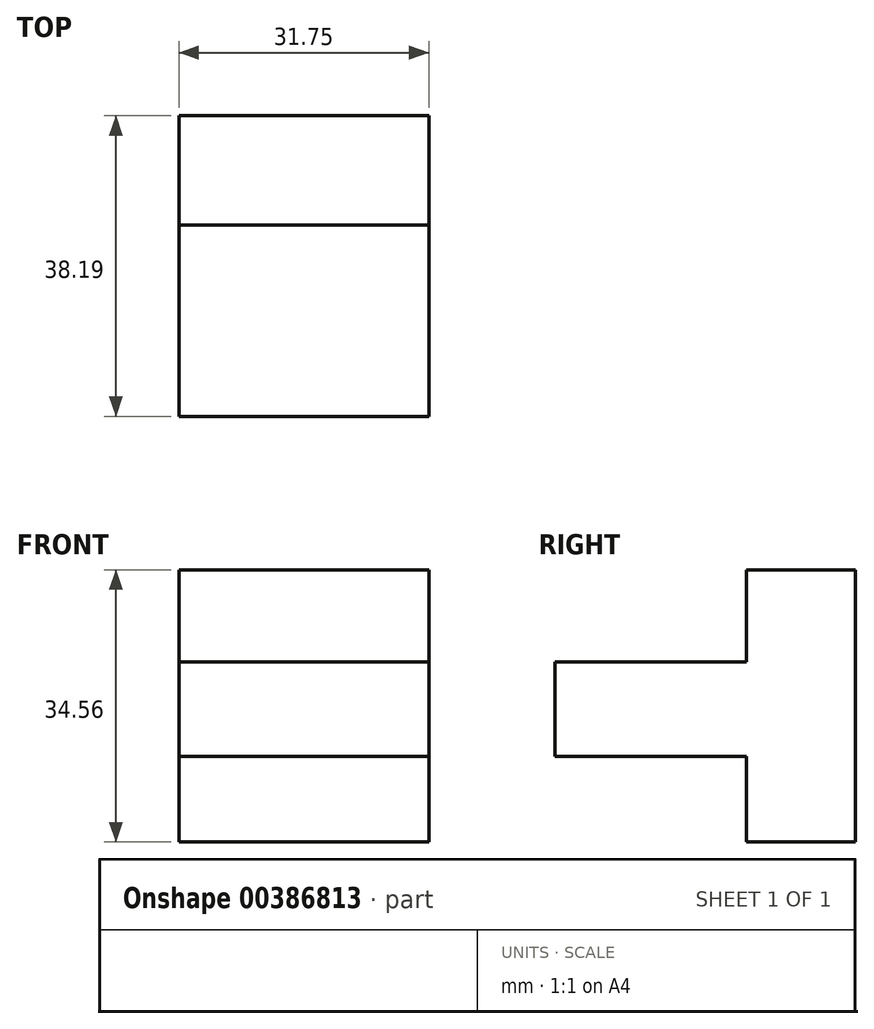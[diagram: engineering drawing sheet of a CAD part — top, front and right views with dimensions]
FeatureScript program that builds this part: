
annotation { "Feature Type Name" : "Feature", "Feature Type Description" : "" }
export const myFeature = defineFeature(function(context is Context, id is Id, definition is map)
    precondition{}
    {
        {
            var Q0;
            Q0=qCreatedBy(makeId("Right.planeOp"),FACE);
            var sketch = newSketch(context, id + "F0", { "sketchPlane" : qUnion([Q0])});
            skLineSegment(sketch, "E0", {"start": v(0, 0) * mm, "end": v(0, 34.56) * mm});
            skLineSegment(sketch, "E1", {"start": v(0, 34.56) * mm, "end": v(-13.87, 34.56) * mm});
            skLineSegment(sketch, "E2", {"start": v(-13.87, 34.56) * mm, "end": v(-13.87, 22.83) * mm});
            skLineSegment(sketch, "E3", {"start": v(-13.87, 22.83) * mm, "end": v(-38.2, 22.83) * mm});
            skLineSegment(sketch, "E4", {"start": v(-38.2, 22.83) * mm, "end": v(-38.2, 10.88) * mm});
            skLineSegment(sketch, "E5", {"start": v(-38.2, 10.88) * mm, "end": v(-13.87, 10.88) * mm});
            skLineSegment(sketch, "E6", {"start": v(-13.87, 10.88) * mm, "end": v(-13.87, 0) * mm});
            skLineSegment(sketch, "E7", {"start": v(-13.87, 0) * mm, "end": v(0, 0) * mm});
            skSolve(sketch);
        }
        {
            var Q0;
            Q0=makeQuery(id+"F0.imprint","IMPRINT",FACE,{"disambiguationData":[TD([[makeQuery(id+"F0.imprint","IMPRINT",EDGE,{"derivedFrom":sQuery(id+"F0.wireOp",EDGE,"E0")}),1.0]])]});
            extrude(context, id + "F1", {"entities" : qUnion([Q0]), "oppositeDirection" : true, "depth" : 31.75 * mm});
        }
    });
